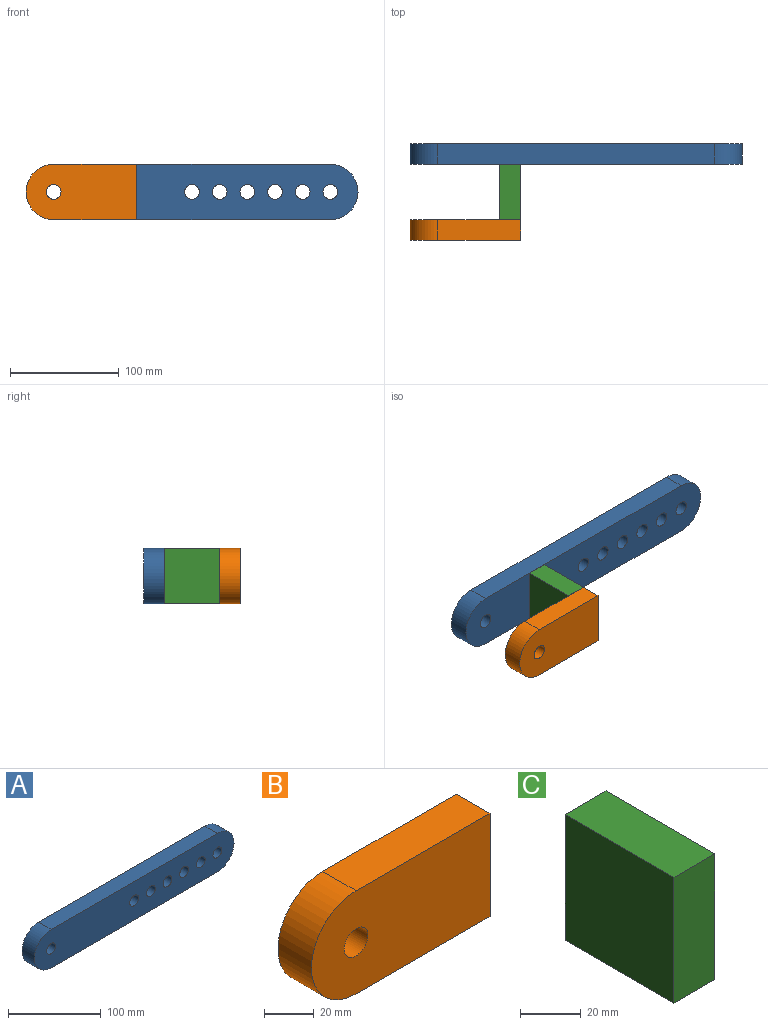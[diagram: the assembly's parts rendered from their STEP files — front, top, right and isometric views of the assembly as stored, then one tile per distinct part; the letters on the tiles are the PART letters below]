
ASSEMBLY  parts=3 mates=4
PART A: 13 faces, bbox 304.8x19.1x50.8 mm
  f0: plane 254x19.05mm, normal (0,0,1), area 4838.7mm2, adj f1,f3,f4,f5
  f1: cylinder r=25.4mm len=50.8mm, axis (0,1,0), area 1520.1mm2, adj f0,f2,f4,f5
  f2: plane 254x19.05mm, normal (0,0,-1), area 4838.7mm2, adj f1,f3,f4,f5
  f3: cylinder r=25.4mm len=50.8mm, axis (0,1,0), area 1520.1mm2, adj f0,f2,f4,f5
  f4: plane 304.8x50.8mm, normal (0,-1,0), area 13929.2mm2, adj f0,f1,f2,f3,f6,f7,f8,f9
  f5: plane 304.8x50.8mm, normal (0,1,0), area 13929.2mm2, adj f0,f1,f2,f3,f6,f7,f8,f9
  f6: cylinder r=6.75mm len=19.05mm, axis (0,-1,0), area 807.5mm2, adj f4,f5
  f7: cylinder r=6.75mm len=19.05mm, axis (0,-1,0), area 807.5mm2, adj f4,f5
  f8: cylinder r=6.75mm len=19.05mm, axis (0,-1,0), area 807.5mm2, adj f4,f5
  f9: cylinder r=6.75mm len=19.05mm, axis (0,-1,0), area 807.5mm2, adj f4,f5
  f10: cylinder r=6.75mm len=19.05mm, axis (0,-1,0), area 807.5mm2, adj f4,f5
  f11: cylinder r=6.75mm len=19.05mm, axis (0,-1,0), area 807.5mm2, adj f4,f5
  f12: cylinder r=6.75mm len=19.05mm, axis (0,-1,0), area 807.5mm2, adj f4,f5
PART B: 7 faces, bbox 101.6x19.1x50.8 mm
  f0: plane 50.8x19.05mm, normal (1,0,0), area 967.7mm2, adj f1,f3,f4,f5
  f1: plane 76.2x19.05mm, normal (0,0,1), area 1451.6mm2, adj f0,f2,f4,f5
  f2: cylinder r=25.4mm len=50.8mm, axis (0,1,0), area 1520.1mm2, adj f1,f3,f4,f5
  f3: plane 76.2x19.05mm, normal (0,0,-1), area 1451.6mm2, adj f0,f2,f4,f5
  f4: plane 101.6x50.8mm, normal (0,-1,0), area 4741.4mm2, adj f0,f1,f2,f3,f6
  f5: plane 101.6x50.8mm, normal (0,1,0), area 4741.4mm2, adj f0,f1,f2,f3,f6
  f6: cylinder r=6.75mm len=19.05mm, axis (0,-1,0), area 807.5mm2, adj f4,f5
PART C: 6 faces, bbox 19.1x50.8x50.8 mm
  f0: plane 50.8x19.05mm, normal (0,1,0), area 967.7mm2, adj f1,f3,f4,f5
  f1: plane 50.8x19.05mm, normal (0,0,1), area 967.7mm2, adj f0,f2,f4,f5
  f2: plane 50.8x19.05mm, normal (0,-1,0), area 967.7mm2, adj f1,f3,f4,f5
  f3: plane 50.8x19.05mm, normal (0,0,-1), area 967.7mm2, adj f0,f2,f4,f5
  f4: plane 50.8x50.8mm, normal (1,0,0), area 2580.6mm2, adj f0,f1,f2,f3
  f5: plane 50.8x50.8mm, normal (-1,0,0), area 2580.6mm2, adj f0,f1,f2,f3
PLACE A at identity fixed
PLACE B rot(axis=(0,1,0),0deg) t=(-101.6,-69.85,0)mm
PLACE C rot(axis=(0,1,0),0deg) t=(-69.85,-34.92,0)mm
MATE fastened C.f2 <-> B.f5  axis (0,-1,0) through (-50.8,-60.32,0)mm
MATE planar C.f1 <-> A.f0  axis (0,0,1) through (-60.33,-34.92,25.4)mm
MATE planar A.f4 <-> C.f0  axis (0,-1,0) through (-2.61,-9.52,0)mm
MATE cylindrical A.f12 <-> B.f2  axis (0,-1,0) through (-127,-9.53,0)mm
